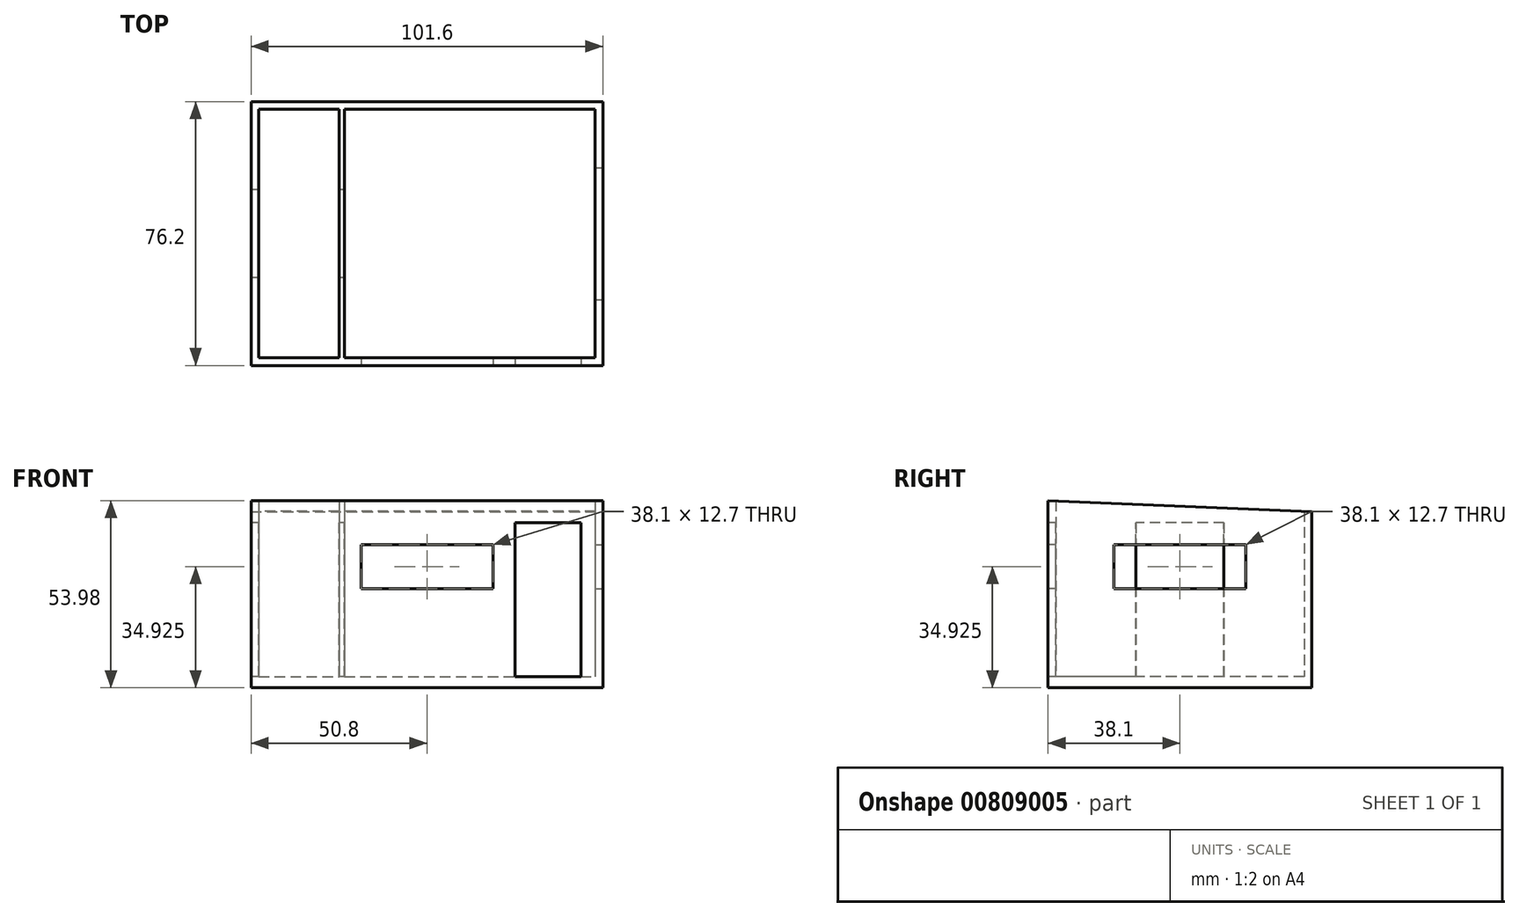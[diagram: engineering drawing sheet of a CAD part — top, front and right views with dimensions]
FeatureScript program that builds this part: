
annotation { "Feature Type Name" : "Feature", "Feature Type Description" : "" }
export const myFeature = defineFeature(function(context is Context, id is Id, definition is map)
    precondition{}
    {
        {
            var Q0;
            Q0=qCreatedBy(makeId("Top.planeOp"),FACE);
            var sketch = newSketch(context, id + "F0", { "sketchPlane" : qUnion([Q0])});
            skLineSegment(sketch, "E0.bottom", {"start": v(-50.8, 38.1) * mm, "end": v(50.8, 38.1) * mm});
            skLineSegment(sketch, "E0.top", {"start": v(-50.8, -38.1) * mm, "end": v(50.8, -38.1) * mm});
            skLineSegment(sketch, "E0.left", {"start": v(-50.8, 38.1) * mm, "end": v(-50.8, -38.1) * mm});
            skLineSegment(sketch, "E0.right", {"start": v(50.8, 38.1) * mm, "end": v(50.8, -38.1) * mm});
            skLineSegment(sketch, "E1", {"start": v(-50.8, 38.1) * mm, "end": v(50.8, -38.1) * mm, "construction": true});
            skLineSegment(sketch, "E2", {"start": v(-50.8, -38.1) * mm, "end": v(50.8, 38.1) * mm, "construction": true});
            skSolve(sketch);
        }
        {
            var Q0;
            Q0 = qSketchRegion(id + "F0", true);
            extrude(context, id + "F1", {"entities" : qUnion([Q0]), "depth" : 3.17 * mm, "offsetDistance" : 25.4 * mm});
        }
        {
            var Q0;
            Q0=makeQuery(id+"F1.opExtrude","CAP_FACE",FACE,{"disambiguationData":[OSD([sQuery(id+"F0.wireOp",EDGE,"E0.bottom"),sQuery(id+"F0.wireOp",EDGE,"E0.top"),sQuery(id+"F0.wireOp",EDGE,"E0.left"),sQuery(id+"F0.wireOp",EDGE,"E0.right")])],"isStart":false});
            var sketch = newSketch(context, id + "F2", { "sketchPlane" : qUnion([Q0])});
            skLineSegment(sketch, "E3.bottom", {"start": v(-50.8, 38.1) * mm, "end": v(50.8, 38.1) * mm});
            skLineSegment(sketch, "E3.top", {"start": v(-50.8, -38.1) * mm, "end": v(50.8, -38.1) * mm});
            skLineSegment(sketch, "E3.left", {"start": v(-50.8, 38.1) * mm, "end": v(-50.8, -38.1) * mm});
            skLineSegment(sketch, "E3.right", {"start": v(50.8, 38.1) * mm, "end": v(50.8, -38.1) * mm});
            skLineSegment(sketch, "E4.bottom", {"start": v(-48.58, 35.88) * mm, "end": v(48.58, 35.88) * mm});
            skLineSegment(sketch, "E4.top", {"start": v(-48.58, -35.88) * mm, "end": v(48.58, -35.88) * mm});
            skLineSegment(sketch, "E4.left", {"start": v(-48.58, 35.88) * mm, "end": v(-48.58, -35.88) * mm});
            skLineSegment(sketch, "E4.right", {"start": v(48.58, 35.88) * mm, "end": v(48.58, -35.88) * mm});
            skLineSegment(sketch, "E5", {"start": v(-48.58, 35.88) * mm, "end": v(48.58, -35.88) * mm, "construction": true});
            skLineSegment(sketch, "E6", {"start": v(48.58, 35.88) * mm, "end": v(-48.58, -35.88) * mm, "construction": true});
            skSolve(sketch);
        }
        {
            var Q0;
            Q0 = qSketchRegion(id + "F2", true);
            extrude(context, id + "F3", {"entities" : qUnion([Q0]), "operationType" : NewBodyOperationType.ADD, "depth" : 50.8 * mm, "offsetDistance" : 25.4 * mm});
        }
        {
            var Q0;
            Q0=makeQuery(id+"F1.opExtrude","CAP_FACE",FACE,{"disambiguationData":[OSD([sQuery(id+"F0.wireOp",EDGE,"E0.bottom"),sQuery(id+"F0.wireOp",EDGE,"E0.top"),sQuery(id+"F0.wireOp",EDGE,"E0.left"),sQuery(id+"F0.wireOp",EDGE,"E0.right")])],"isStart":false});
            var sketch = newSketch(context, id + "F4", { "sketchPlane" : qUnion([Q0])});
            skLineSegment(sketch, "E7.bottom", {"start": v(-25.4, 35.88) * mm, "end": v(-23.81, 35.88) * mm});
            skLineSegment(sketch, "E7.top", {"start": v(-25.4, -35.88) * mm, "end": v(-23.81, -35.88) * mm});
            skLineSegment(sketch, "E7.left", {"start": v(-25.4, 35.88) * mm, "end": v(-25.4, -35.88) * mm});
            skLineSegment(sketch, "E7.right", {"start": v(-23.81, 35.88) * mm, "end": v(-23.81, -35.88) * mm});
            skSolve(sketch);
        }
        {
            var Q0;
            Q0 = qSketchRegion(id + "F4", true);
            extrude(context, id + "F5", {"entities" : qUnion([Q0]), "operationType" : NewBodyOperationType.ADD, "depth" : 50.8 * mm, "offsetDistance" : 25.4 * mm});
        }
        {
            var Q0;
            Q0=makeQuery(id+"F3.boolean.opBoolean","MERGE",FACE,{"derivedFrom":[makeQuery(id+"F1.opExtrude","SWEPT_FACE",FACE,{"disambiguationData":[OSD([sQuery(id+"F0.wireOp",EDGE,"E0.top")])]}),makeQuery(id+"F3.opExtrude","SWEPT_FACE",FACE,{"disambiguationData":[OSD([sQuery(id+"F2.wireOp",EDGE,"E3.top")])]})]});
            var sketch = newSketch(context, id + "F6", { "sketchPlane" : qUnion([Q0])});
            skLineSegment(sketch, "E8.bottom", {"start": v(25.4, 47.62) * mm, "end": v(44.45, 47.62) * mm});
            skLineSegment(sketch, "E8.top", {"start": v(25.4, 3.18) * mm, "end": v(44.45, 3.18) * mm});
            skLineSegment(sketch, "E8.left", {"start": v(25.4, 47.62) * mm, "end": v(25.4, 3.17) * mm});
            skLineSegment(sketch, "E8.right", {"start": v(44.45, 47.63) * mm, "end": v(44.45, 3.18) * mm});
            skLineSegment(sketch, "E9.bottom", {"start": v(-19.05, 41.27) * mm, "end": v(19.05, 41.27) * mm});
            skLineSegment(sketch, "E9.top", {"start": v(-19.05, 28.57) * mm, "end": v(19.05, 28.57) * mm});
            skLineSegment(sketch, "E9.left", {"start": v(-19.05, 41.27) * mm, "end": v(-19.05, 28.57) * mm});
            skLineSegment(sketch, "E9.right", {"start": v(19.05, 41.27) * mm, "end": v(19.05, 28.57) * mm});
            skLineSegment(sketch, "E10", {"start": v(0, 2.24) * mm, "end": v(0, 28.57) * mm, "construction": true});
            skSolve(sketch);
        }
        {
            var Q0;
            Q0 = qSketchRegion(id + "F6", true);
            extrude(context, id + "F7", {"entities" : qUnion([Q0]), "operationType" : NewBodyOperationType.REMOVE, "oppositeDirection" : true, "depth" : 25.4 * mm, "offsetDistance" : 25.4 * mm});
        }
        {
            var Q0;
            Q0=makeQuery(id+"F3.boolean.opBoolean","MERGE",FACE,{"derivedFrom":[makeQuery(id+"F1.opExtrude","SWEPT_FACE",FACE,{"disambiguationData":[OSD([sQuery(id+"F0.wireOp",EDGE,"E0.right")])]}),makeQuery(id+"F3.opExtrude","SWEPT_FACE",FACE,{"disambiguationData":[OSD([sQuery(id+"F2.wireOp",EDGE,"E3.right")])]})]});
            var sketch = newSketch(context, id + "F8", { "sketchPlane" : qUnion([Q0])});
            skLineSegment(sketch, "E11.bottom", {"start": v(-19.05, 41.27) * mm, "end": v(19.05, 41.27) * mm});
            skLineSegment(sketch, "E11.top", {"start": v(-19.05, 28.57) * mm, "end": v(19.05, 28.57) * mm});
            skLineSegment(sketch, "E11.left", {"start": v(-19.05, 41.27) * mm, "end": v(-19.05, 28.57) * mm});
            skLineSegment(sketch, "E11.right", {"start": v(19.05, 41.27) * mm, "end": v(19.05, 28.57) * mm});
            skLineSegment(sketch, "E12", {"start": v(0, 0) * mm, "end": v(0, 28.57) * mm, "construction": true});
            skSolve(sketch);
        }
        {
            var Q0;
            Q0 = qSketchRegion(id + "F8", true);
            extrude(context, id + "F9", {"entities" : qUnion([Q0]), "operationType" : NewBodyOperationType.REMOVE, "oppositeDirection" : true, "depth" : 25.4 * mm, "offsetDistance" : 25.4 * mm});
        }
        {
            var Q0;
            Q0=makeQuery(id+"F3.boolean.opBoolean","MERGE",FACE,{"derivedFrom":[makeQuery(id+"F1.opExtrude","SWEPT_FACE",FACE,{"disambiguationData":[OSD([sQuery(id+"F0.wireOp",EDGE,"E0.right")])]}),makeQuery(id+"F3.opExtrude","SWEPT_FACE",FACE,{"disambiguationData":[OSD([sQuery(id+"F2.wireOp",EDGE,"E3.right")])]})]});
            var sketch = newSketch(context, id + "F10", { "sketchPlane" : qUnion([Q0])});
            skLineSegment(sketch, "E13", {"start": v(-38.1, 53.98) * mm, "end": v(38.1, 50.8) * mm});
            skLineSegment(sketch, "E14", {"start": v(38.1, 50.8) * mm, "end": v(38.1, 53.98) * mm});
            skLineSegment(sketch, "E15", {"start": v(38.1, 53.98) * mm, "end": v(-38.1, 53.98) * mm});
            skLineSegment(sketch, "E16", {"start": v(-38.1, 53.98) * mm, "end": v(-38.1, 53.98) * mm});
            skSolve(sketch);
        }
        {
            var Q0;
            Q0 = qSketchRegion(id + "F10", true);
            var Q1;
            Q1=makeQuery(id+"F3.boolean.opBoolean","MERGE",FACE,{"derivedFrom":[makeQuery(id+"F1.opExtrude","SWEPT_FACE",FACE,{"disambiguationData":[OSD([sQuery(id+"F0.wireOp",EDGE,"E0.left")])]}),makeQuery(id+"F3.opExtrude","SWEPT_FACE",FACE,{"disambiguationData":[OSD([sQuery(id+"F2.wireOp",EDGE,"E3.left")])]})]});
            extrude(context, id + "F11", {"entities" : qUnion([Q0]), "operationType" : NewBodyOperationType.REMOVE, "endBound" : BoundingType.UP_TO_SURFACE, "oppositeDirection" : true, "depth" : 25.4 * mm, "endBoundEntityFace" : qUnion([Q1]), "offsetDistance" : 25.4 * mm});
        }
        {
            var Q0;
            Q0=makeQuery(id+"F3.boolean.opBoolean","MERGE",FACE,{"derivedFrom":[makeQuery(id+"F1.opExtrude","SWEPT_FACE",FACE,{"disambiguationData":[OSD([sQuery(id+"F0.wireOp",EDGE,"E0.left")])]}),makeQuery(id+"F3.opExtrude","SWEPT_FACE",FACE,{"disambiguationData":[OSD([sQuery(id+"F2.wireOp",EDGE,"E3.left")])]})]});
            var sketch = newSketch(context, id + "F12", { "sketchPlane" : qUnion([Q0])});
            skLineSegment(sketch, "E17.bottom", {"start": v(-12.7, 47.63) * mm, "end": v(12.7, 47.63) * mm});
            skLineSegment(sketch, "E17.top", {"start": v(-12.7, 3.17) * mm, "end": v(12.7, 3.18) * mm});
            skLineSegment(sketch, "E17.left", {"start": v(-12.7, 47.63) * mm, "end": v(-12.7, 3.18) * mm});
            skLineSegment(sketch, "E17.right", {"start": v(12.7, 47.63) * mm, "end": v(12.7, 3.18) * mm});
            skLineSegment(sketch, "E18", {"start": v(0, 0) * mm, "end": v(0, 3.18) * mm, "construction": true});
            skSolve(sketch);
        }
        {
            var Q0;
            Q0 = qSketchRegion(id + "F12", true);
            extrude(context, id + "F13", {"entities" : qUnion([Q0]), "operationType" : NewBodyOperationType.REMOVE, "oppositeDirection" : true, "depth" : 76.2 * mm, "offsetDistance" : 25.4 * mm});
        }
    });
